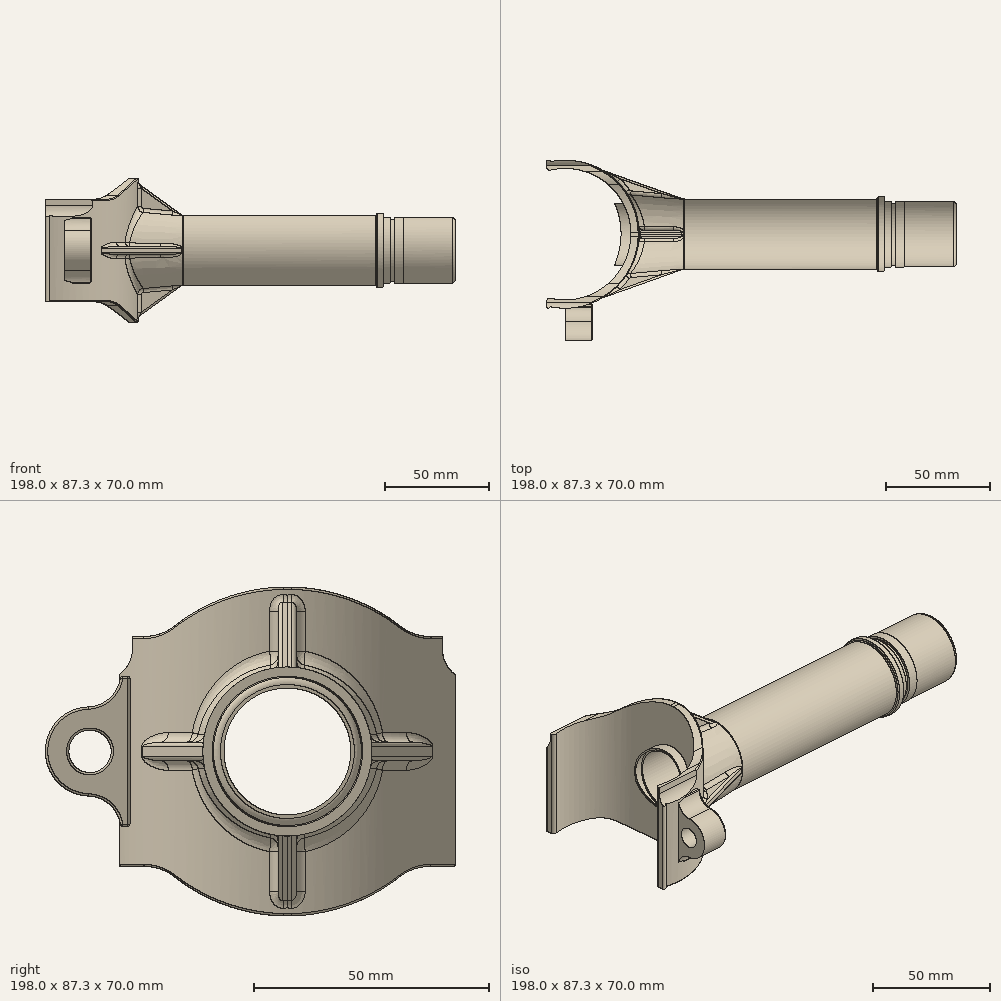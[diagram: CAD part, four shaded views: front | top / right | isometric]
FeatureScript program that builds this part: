
annotation { "Feature Type Name" : "Feature", "Feature Type Description" : "" }
export const myFeature = defineFeature(function(context is Context, id is Id, definition is map)
    precondition{}
    {
        {
            var Q0;
            Q0=qCreatedBy(makeId("Right.planeOp"),FACE);
            var sketch = newSketch(context, id + "F0", { "sketchPlane" : qUnion([Q0])});
            skLineSegment(sketch, "E0", {"start": v(0, 105.09) * mm, "end": v(0, -109.38) * mm, "construction": true});
            skLineSegment(sketch, "E1", {"start": v(-124.9, 0) * mm, "end": v(126.38, 0) * mm, "construction": true});
            skLineSegment(sketch, "E2.0", {"start": v(-42, 105.09) * mm, "end": v(-42, -109.38) * mm, "construction": true});
            skArc(sketch, "E3", {"start": v(-42.29, 9.5) * mm, "mid": v(-51.5, 0) * mm, "end": v(-42.29, -9.5) * mm});
            skLineSegment(sketch, "E4.0", {"start": v(-124.9, 24.5) * mm, "end": v(-30.22, 24.5) * mm});
            skLineSegment(sketch, "E5.MirrorCS", {"start": v(-124.9, -24.5) * mm, "end": v(-30.22, -24.5) * mm});
            skLineSegment(sketch, "E6.0", {"start": v(-124.9, -3.7) * mm, "end": v(126.38, -3.7) * mm, "construction": true});
            skArc(sketch, "E7.trimOffspring", {"start": v(24.01, 26.66) * mm, "mid": v(0, 35.01) * mm, "end": v(-24.01, 26.66) * mm});
            skPoint(sketch, "E8.newPointB", {"position": v(126.68, 24.5) * mm});
            skArc(sketch, "E8.filletArc", {"start": v(-30.22, 24.5) * mm, "mid": v(-26.93, 25.05) * mm, "end": v(-24.01, 26.66) * mm});
            skArc(sketch, "E9.MirrorCS", {"start": v(30.22, 24.5) * mm, "mid": v(26.93, 25.05) * mm, "end": v(24.01, 26.66) * mm});
            skLineSegment(sketch, "E10.MirrorCS", {"start": v(124.9, 24.5) * mm, "end": v(30.22, 24.5) * mm});
            skLineSegment(sketch, "E11", {"start": v(-68.14, 24.5) * mm, "end": v(-68.14, 50.23) * mm});
            skLineSegment(sketch, "E12", {"start": v(-68.14, 50.23) * mm, "end": v(68.14, 50.23) * mm});
            skLineSegment(sketch, "E13.MirrorCS", {"start": v(68.14, 24.5) * mm, "end": v(68.14, 50.23) * mm});
            skArc(sketch, "E14.MirrorCS", {"start": v(30.22, -24.5) * mm, "mid": v(26.93, -25.05) * mm, "end": v(24.01, -26.66) * mm});
            skArc(sketch, "E15.MirrorCS", {"start": v(24.01, -26.66) * mm, "mid": v(0, -35.01) * mm, "end": v(-24.01, -26.66) * mm});
            skArc(sketch, "E16.MirrorCS", {"start": v(-30.22, -24.5) * mm, "mid": v(-26.93, -25.05) * mm, "end": v(-24.01, -26.66) * mm});
            skLineSegment(sketch, "E17.MirrorCS", {"start": v(-68.14, -24.5) * mm, "end": v(-68.14, -50.23) * mm});
            skLineSegment(sketch, "E18.MirrorCS", {"start": v(-68.14, -50.23) * mm, "end": v(68.14, -50.23) * mm});
            skLineSegment(sketch, "E19.MirrorCS", {"start": v(68.14, -24.5) * mm, "end": v(68.14, -50.23) * mm});
            skLineSegment(sketch, "E20.trimOffspring", {"start": v(30.22, -24.5) * mm, "end": v(126.68, -24.5) * mm});
            skLineSegment(sketch, "E21.0", {"start": v(-33.5, 15.5) * mm, "end": v(-33.5, -15.5) * mm});
            skLineSegment(sketch, "E22.0", {"start": v(-35.07, 16) * mm, "end": v(-34, 16) * mm});
            skPoint(sketch, "E23.visualSharp", {"position": v(-35.5, 6.93) * mm});
            skArc(sketch, "E23.filletArc", {"start": v(-42.29, 9.5) * mm, "mid": v(-37.81, 11.3) * mm, "end": v(-35.56, 15.57) * mm});
            skArc(sketch, "E24.filletArc", {"start": v(-35.07, 16) * mm, "mid": v(-35.4, 15.88) * mm, "end": v(-35.56, 15.57) * mm});
            skArc(sketch, "E25.filletArc", {"start": v(-33.5, 15.5) * mm, "mid": v(-33.65, 15.85) * mm, "end": v(-34, 16) * mm});
            skArc(sketch, "E26.MirrorCS", {"start": v(-42.29, -9.5) * mm, "mid": v(-37.81, -11.3) * mm, "end": v(-35.56, -15.57) * mm});
            skArc(sketch, "E27.MirrorCS", {"start": v(-35.07, -16) * mm, "mid": v(-35.4, -15.88) * mm, "end": v(-35.56, -15.57) * mm});
            skLineSegment(sketch, "E28.MirrorCS", {"start": v(-35.07, -16) * mm, "end": v(-34, -16) * mm});
            skArc(sketch, "E29.MirrorCS", {"start": v(-33.5, -15.5) * mm, "mid": v(-33.65, -15.85) * mm, "end": v(-34, -16) * mm});
            skLineSegment(sketch, "E30.trimOffspring", {"start": v(-33.5, -24.5) * mm, "end": v(-33.5, -109.38) * mm});
            skCircle(sketch, "E31", {"center": v(-42, 0) * mm, "radius": 4.5 * mm});
            skArc(sketch, "E32.MirrorCS", {"start": v(33.5, 15.5) * mm, "mid": v(33.65, 15.85) * mm, "end": v(34, 16) * mm});
            skArc(sketch, "E33.MirrorCS", {"start": v(35.07, 16) * mm, "mid": v(35.4, 15.88) * mm, "end": v(35.56, 15.57) * mm});
            skArc(sketch, "E34.MirrorCS", {"start": v(35.07, -16) * mm, "mid": v(35.4, -15.88) * mm, "end": v(35.56, -15.57) * mm});
            skLineSegment(sketch, "E35.MirrorCS", {"start": v(35.07, 16) * mm, "end": v(34, 16) * mm});
            skLineSegment(sketch, "E36.MirrorCS", {"start": v(35.07, -16) * mm, "end": v(34, -16) * mm});
            skArc(sketch, "E37.MirrorCS", {"start": v(33.5, -15.5) * mm, "mid": v(33.65, -15.85) * mm, "end": v(34, -16) * mm});
            skCircle(sketch, "E38.MirrorC", {"center": v(42, 0) * mm, "radius": 4.5 * mm});
            skPoint(sketch, "E39.MirrorP", {"position": v(35.5, 6.93) * mm});
            skLineSegment(sketch, "E40.MirrorCS", {"start": v(33.5, 15.5) * mm, "end": v(33.5, -15.5) * mm});
            skArc(sketch, "E41.MirrorCS", {"start": v(42.29, 9.5) * mm, "mid": v(37.81, 11.3) * mm, "end": v(35.56, 15.57) * mm});
            skArc(sketch, "E42.MirrorCS", {"start": v(42.29, -9.5) * mm, "mid": v(37.81, -11.3) * mm, "end": v(35.56, -15.57) * mm});
            skArc(sketch, "E43.MirrorCS", {"start": v(42.29, 9.5) * mm, "mid": v(51.5, 0) * mm, "end": v(42.29, -9.5) * mm});
            skSolve(sketch);
        }
        {
            var Q0;
            Q0=qCreatedBy(makeId("Top.planeOp"),FACE);
            var sketch = newSketch(context, id + "F1", { "sketchPlane" : qUnion([Q0])});
            skLineSegment(sketch, "E44", {"start": v(-75.74, 0) * mm, "end": v(95.85, 0) * mm, "construction": true});
            skLineSegment(sketch, "E45", {"start": v(0, 79.62) * mm, "end": v(0, -83.5) * mm, "construction": true});
            skArc(sketch, "E46", {"start": v(-7.02, -30.96) * mm, "mid": v(31.75, 0) * mm, "end": v(-7.02, 30.96) * mm});
            skArc(sketch, "E47.0", {"start": v(-8.99, 34.6) * mm, "mid": v(-8.99, 34.6) * mm, "end": v(-9, 34.6) * mm});
            skLineSegment(sketch, "E48.0", {"start": v(-8, 79.62) * mm, "end": v(-8, -83.5) * mm, "construction": true});
            skLineSegment(sketch, "E49.0", {"start": v(-75.74, 34.77) * mm, "end": v(95.85, 34.77) * mm, "construction": true});
            skArc(sketch, "E50", {"start": v(-7.04, 35.05) * mm, "mid": v(-8.22, 35.74) * mm, "end": v(-8.99, 34.6) * mm});
            skLineSegment(sketch, "E51", {"start": v(-8.85, 32.33) * mm, "end": v(-9, 34.7) * mm});
            skArc(sketch, "E52.trimOffspring", {"start": v(-9, -34.6) * mm, "mid": v(-8.99, -34.6) * mm, "end": v(-8.99, -34.6) * mm});
            skLineSegment(sketch, "E53.MirrorCS", {"start": v(-8.85, -32.33) * mm, "end": v(-9, -34.7) * mm});
            skArc(sketch, "E54.MirrorC", {"start": v(-7.04, -35.05) * mm, "mid": v(-8.17, -35.76) * mm, "end": v(-9, -34.7) * mm});
            skPoint(sketch, "E55.newPointA", {"position": v(-8.7, 30) * mm});
            skArc(sketch, "E55.filletArc", {"start": v(-8.85, 32.33) * mm, "mid": v(-8.25, 31.23) * mm, "end": v(-7.02, 30.96) * mm});
            skPoint(sketch, "E56.newPointA", {"position": v(-8.7, -30) * mm});
            skArc(sketch, "E56.filletArc", {"start": v(-7.02, -30.96) * mm, "mid": v(-8.25, -31.23) * mm, "end": v(-8.85, -32.33) * mm});
            skArc(sketch, "E57.trimOffspring", {"start": v(-7.04, -35.05) * mm, "mid": v(35.75, 0) * mm, "end": v(-7.04, 35.05) * mm});
            skSolve(sketch);
        }
        {
            var Q0;
            Q0=makeQuery(id+"F1.imprint","IMPRINT",FACE,{"disambiguationData":[TD([[makeQuery(id+"F1.imprint","IMPRINT",EDGE,{"derivedFrom":sQuery(id+"F1.wireOp",EDGE,"E46")}),-1.0]])]});
            extrude(context, id + "F2", {"entities" : qUnion([Q0]), "endBound" : BoundingType.SYMMETRIC, "depth" : 70 * mm, "offsetDistance" : 25 * mm});
        }
        {
            var Q0;
            Q0=makeQuery(id+"F0.imprint","IMPRINT",FACE,{"disambiguationData":[TD([[makeQuery(id+"F0.imprint","IMPRINT",EDGE,{"derivedFrom":sQuery(id+"F0.wireOp",EDGE,"E7.trimOffspring")}),-1.0]])]});
            var Q1;
            {var subQ0=sQuery(id+"F0.wireOp",EDGE,"E14.MirrorCS");Q1=makeQuery(id+"F0.imprint","IMPRINT",FACE,{"disambiguationData":[TD([[makeQuery(id+"F0.imprint","IMPRINT",EDGE,{"derivedFrom":subQ0}),1.0]])]});}
            var Q2;
            {var subQ5=sQuery(id+"F0.wireOp",EDGE,"E17.MirrorCS");Q2=makeQuery(id+"F0.imprint","IMPRINT",FACE,{"disambiguationData":[TD([[makeQuery(id+"F0.imprint","IMPRINT",EDGE,{"derivedFrom":subQ5}),1.0]])]});}
            extrude(context, id + "F3", {"entities" : qUnion([Q0, Q1, Q2]), "operationType" : NewBodyOperationType.REMOVE, "endBound" : BoundingType.SYMMETRIC, "depth" : 100 * mm, "offsetDistance" : 25 * mm});
        }
        {
            var Q0;
            Q0=makeQuery(id+"F0.imprint","IMPRINT",FACE,{"disambiguationData":[TD([[makeQuery(id+"F0.imprint","IMPRINT",EDGE,{"derivedFrom":sQuery(id+"F0.wireOp",EDGE,"E3")}),1.0]])]});
            var Q1;
            Q1=makeQuery(id+"F0.imprint","IMPRINT",FACE,{"disambiguationData":[TD([[makeQuery(id+"F0.imprint","IMPRINT",EDGE,{"derivedFrom":sQuery(id+"F0.wireOp",EDGE,"E32.MirrorCS")}),-1.0]])]});
            extrude(context, id + "F4", {"entities" : qUnion([Q0, Q1]), "operationType" : NewBodyOperationType.ADD, "depth" : 13 * mm, "offsetDistance" : 25 * mm});
        }
        {
            var Q0;
            Q0=makeQuery(id+"F4.opExtrude","CAP_FACE",FACE,{"disambiguationData":[OSD([sQuery(id+"F0.wireOp",EDGE,"E3"),sQuery(id+"F0.wireOp",EDGE,"E21.0"),sQuery(id+"F0.wireOp",EDGE,"E22.0"),sQuery(id+"F0.wireOp",EDGE,"E23.filletArc"),sQuery(id+"F0.wireOp",EDGE,"E24.filletArc"),sQuery(id+"F0.wireOp",EDGE,"E25.filletArc"),sQuery(id+"F0.wireOp",EDGE,"E26.MirrorCS"),sQuery(id+"F0.wireOp",EDGE,"E27.MirrorCS"),sQuery(id+"F0.wireOp",EDGE,"E28.MirrorCS"),sQuery(id+"F0.wireOp",EDGE,"E29.MirrorCS"),sQuery(id+"F0.wireOp",EDGE,"E31")])],"isStart":false});
            var Q1;
            Q1=makeQuery(id+"F4.opExtrude","CAP_FACE",FACE,{"disambiguationData":[OSD([sQuery(id+"F0.wireOp",EDGE,"E32.MirrorCS"),sQuery(id+"F0.wireOp",EDGE,"E33.MirrorCS"),sQuery(id+"F0.wireOp",EDGE,"E34.MirrorCS"),sQuery(id+"F0.wireOp",EDGE,"E35.MirrorCS"),sQuery(id+"F0.wireOp",EDGE,"E36.MirrorCS"),sQuery(id+"F0.wireOp",EDGE,"E37.MirrorCS"),sQuery(id+"F0.wireOp",EDGE,"E38.MirrorC"),sQuery(id+"F0.wireOp",EDGE,"E40.MirrorCS"),sQuery(id+"F0.wireOp",EDGE,"E41.MirrorCS"),sQuery(id+"F0.wireOp",EDGE,"E42.MirrorCS"),sQuery(id+"F0.wireOp",EDGE,"E43.MirrorCS")])],"isStart":false});
            fillet(context, id + "F5", {"entities" : qUnion([Q0, Q1]), "radius" : 0.5 * mm, "tangentPropagation" : true, "allowEdgeOverflow" : false});
        }
        {
            var Q0;
            Q0=qCreatedBy(makeId("Right.planeOp"),FACE);
            var sketch = newSketch(context, id + "F6", { "sketchPlane" : qUnion([Q0])});
            skLineSegment(sketch, "E58", {"start": v(0, 44.7) * mm, "end": v(0, -6.12) * mm, "construction": true});
            skLineSegment(sketch, "E59", {"start": v(-3.2, 0) * mm, "end": v(58.54, 0) * mm, "construction": true});
            skArc(sketch, "E60", {"start": v(33, 21.71) * mm, "mid": v(33.8, 18.54) * mm, "end": v(36, 16.13) * mm});
            skLineSegment(sketch, "E61.0", {"start": v(36, 24.5) * mm, "end": v(36, 16.13) * mm});
            skLineSegment(sketch, "E62.trimOffspring", {"start": v(33, 24.5) * mm, "end": v(36, 24.5) * mm});
            skLineSegment(sketch, "E63", {"start": v(33, 21.71) * mm, "end": v(33, 24.5) * mm});
            skLineSegment(sketch, "E64.MirrorCS", {"start": v(-36, 24.5) * mm, "end": v(-36, 16.13) * mm});
            skArc(sketch, "E65.MirrorCS", {"start": v(-33, 21.71) * mm, "mid": v(-33.8, 18.54) * mm, "end": v(-36, 16.13) * mm});
            skLineSegment(sketch, "E66.MirrorCS", {"start": v(-33, 24.5) * mm, "end": v(-36, 24.5) * mm});
            skLineSegment(sketch, "E67.MirrorCS", {"start": v(-33, 21.71) * mm, "end": v(-33, 24.5) * mm});
            skSolve(sketch);
        }
        {
            var Q0;
            Q0=makeQuery(id+"F6.imprint","IMPRINT",FACE,{"disambiguationData":[TD([[makeQuery(id+"F6.imprint","IMPRINT",EDGE,{"derivedFrom":sQuery(id+"F6.wireOp",EDGE,"E64.MirrorCS")}),1.0]])]});
            var Q1;
            Q1=makeQuery(id+"F6.imprint","IMPRINT",FACE,{"disambiguationData":[TD([[makeQuery(id+"F6.imprint","IMPRINT",EDGE,{"derivedFrom":sQuery(id+"F6.wireOp",EDGE,"E60")}),1.0]])]});
            extrude(context, id + "F7", {"entities" : qUnion([Q0, Q1]), "operationType" : NewBodyOperationType.REMOVE, "endBound" : BoundingType.SYMMETRIC, "depth" : 100 * mm, "offsetDistance" : 25 * mm});
        }
        {
            var Q0;
            Q0=makeQuery(id+"F7.boolean.opBoolean","COPY",EDGE,{"derivedFrom":makeQuery(id+"F7.opExtrude","SWEPT_EDGE",EDGE,{"disambiguationData":[OSD([sQuery(id+"F6.wireOp",EDGE,"E66.MirrorCS"),sQuery(id+"F6.wireOp",EDGE,"E67.MirrorCS")])]})});
            var Q1;
            Q1=makeQuery(id+"F3.boolean.opBoolean","INTERSECT",EDGE,{"derivedFrom":[makeQuery(id+"F2.opExtrude","SWEPT_FACE",FACE,{"disambiguationData":[OSD([sQuery(id+"F1.wireOp",EDGE,"E57.trimOffspring")])]}),makeQuery(id+"F3.opExtrude","SWEPT_FACE",FACE,{"disambiguationData":[OSD([sQuery(id+"F0.wireOp",EDGE,"E4.0")])]})]});
            var Q2;
            Q2=makeQuery(id+"F3.boolean.opBoolean","INTERSECT",EDGE,{"derivedFrom":[makeQuery(id+"F2.opExtrude","SWEPT_FACE",FACE,{"disambiguationData":[OSD([sQuery(id+"F1.wireOp",EDGE,"E57.trimOffspring")])]}),makeQuery(id+"F3.opExtrude","SWEPT_FACE",FACE,{"disambiguationData":[OSD([sQuery(id+"F0.wireOp",EDGE,"E8.filletArc")])]})]});
            var Q3;
            Q3=makeQuery(id+"F2.opExtrude","CAP_EDGE",EDGE,{"disambiguationData":[OSD([sQuery(id+"F1.wireOp",EDGE,"E57.trimOffspring")])],"isStart":false});
            var Q4;
            Q4=makeQuery(id+"F3.boolean.opBoolean","INTERSECT",EDGE,{"disambiguationData":[OD(0.0)],"derivedFrom":[makeQuery(id+"F2.opExtrude","SWEPT_FACE",FACE,{"disambiguationData":[OSD([sQuery(id+"F1.wireOp",EDGE,"E57.trimOffspring")])]}),makeQuery(id+"F3.opExtrude","SWEPT_FACE",FACE,{"disambiguationData":[OSD([sQuery(id+"F0.wireOp",EDGE,"E7.trimOffspring")])]})]});
            var Q5;
            Q5=makeQuery(id+"F3.boolean.opBoolean","INTERSECT",EDGE,{"disambiguationData":[OD(1.0)],"derivedFrom":[makeQuery(id+"F2.opExtrude","SWEPT_FACE",FACE,{"disambiguationData":[OSD([sQuery(id+"F1.wireOp",EDGE,"E57.trimOffspring")])]}),makeQuery(id+"F3.opExtrude","SWEPT_FACE",FACE,{"disambiguationData":[OSD([sQuery(id+"F0.wireOp",EDGE,"E7.trimOffspring")])]})]});
            var Q6;
            Q6=makeQuery(id+"F3.boolean.opBoolean","INTERSECT",EDGE,{"derivedFrom":[makeQuery(id+"F2.opExtrude","SWEPT_FACE",FACE,{"disambiguationData":[OSD([sQuery(id+"F1.wireOp",EDGE,"E57.trimOffspring")])]}),makeQuery(id+"F3.opExtrude","SWEPT_FACE",FACE,{"disambiguationData":[OSD([sQuery(id+"F0.wireOp",EDGE,"E9.MirrorCS")])]})]});
            var Q7;
            Q7=makeQuery(id+"F3.boolean.opBoolean","INTERSECT",EDGE,{"derivedFrom":[makeQuery(id+"F2.opExtrude","SWEPT_FACE",FACE,{"disambiguationData":[OSD([sQuery(id+"F1.wireOp",EDGE,"E57.trimOffspring")])]}),makeQuery(id+"F3.opExtrude","SWEPT_FACE",FACE,{"disambiguationData":[OSD([sQuery(id+"F0.wireOp",EDGE,"E10.MirrorCS")])]})]});
            var Q8;
            Q8=makeQuery(id+"F7.boolean.opBoolean","COPY",EDGE,{"derivedFrom":makeQuery(id+"F7.opExtrude","SWEPT_EDGE",EDGE,{"disambiguationData":[OSD([sQuery(id+"F6.wireOp",EDGE,"E62.trimOffspring"),sQuery(id+"F6.wireOp",EDGE,"E63")])]})});
            var Q9;
            Q9=makeQuery(id+"FyGXZyxvwHZdhN8_1.1.F7.boolean.opBoolean","COPY",EDGE,{"derivedFrom":makeQuery(id+"FyGXZyxvwHZdhN8_1.1.F7.opExtrude","SWEPT_EDGE",EDGE,{"disambiguationData":[OSD([sQuery(id+"F6.wireOp",EDGE,"E66.MirrorCS"),sQuery(id+"F6.wireOp",EDGE,"E67.MirrorCS")])]})});
            var Q10;
            Q10=makeQuery(id+"F3.boolean.opBoolean","INTERSECT",EDGE,{"derivedFrom":[makeQuery(id+"F2.opExtrude","SWEPT_FACE",FACE,{"disambiguationData":[OSD([sQuery(id+"F1.wireOp",EDGE,"E57.trimOffspring")])]}),makeQuery(id+"F3.opExtrude","SWEPT_FACE",FACE,{"disambiguationData":[OSD([sQuery(id+"F0.wireOp",EDGE,"E5.MirrorCS")])]})]});
            var Q11;
            Q11=makeQuery(id+"F3.boolean.opBoolean","INTERSECT",EDGE,{"derivedFrom":[makeQuery(id+"F2.opExtrude","SWEPT_FACE",FACE,{"disambiguationData":[OSD([sQuery(id+"F1.wireOp",EDGE,"E57.trimOffspring")])]}),makeQuery(id+"F3.opExtrude","SWEPT_FACE",FACE,{"disambiguationData":[OSD([sQuery(id+"F0.wireOp",EDGE,"E16.MirrorCS")])]})]});
            var Q12;
            Q12=makeQuery(id+"F3.boolean.opBoolean","INTERSECT",EDGE,{"disambiguationData":[OD(1.0)],"derivedFrom":[makeQuery(id+"F2.opExtrude","SWEPT_FACE",FACE,{"disambiguationData":[OSD([sQuery(id+"F1.wireOp",EDGE,"E57.trimOffspring")])]}),makeQuery(id+"F3.opExtrude","SWEPT_FACE",FACE,{"disambiguationData":[OSD([sQuery(id+"F0.wireOp",EDGE,"E15.MirrorCS")])]})]});
            var Q13;
            Q13=makeQuery(id+"F2.opExtrude","CAP_EDGE",EDGE,{"disambiguationData":[OSD([sQuery(id+"F1.wireOp",EDGE,"E57.trimOffspring")])],"isStart":true});
            var Q14;
            Q14=makeQuery(id+"F3.boolean.opBoolean","INTERSECT",EDGE,{"disambiguationData":[OD(0.0)],"derivedFrom":[makeQuery(id+"F2.opExtrude","SWEPT_FACE",FACE,{"disambiguationData":[OSD([sQuery(id+"F1.wireOp",EDGE,"E57.trimOffspring")])]}),makeQuery(id+"F3.opExtrude","SWEPT_FACE",FACE,{"disambiguationData":[OSD([sQuery(id+"F0.wireOp",EDGE,"E15.MirrorCS")])]})]});
            var Q15;
            Q15=makeQuery(id+"F3.boolean.opBoolean","INTERSECT",EDGE,{"derivedFrom":[makeQuery(id+"F2.opExtrude","SWEPT_FACE",FACE,{"disambiguationData":[OSD([sQuery(id+"F1.wireOp",EDGE,"E57.trimOffspring")])]}),makeQuery(id+"F3.opExtrude","SWEPT_FACE",FACE,{"disambiguationData":[OSD([sQuery(id+"F0.wireOp",EDGE,"E14.MirrorCS")])]})]});
            var Q16;
            Q16=makeQuery(id+"F3.boolean.opBoolean","INTERSECT",EDGE,{"derivedFrom":[makeQuery(id+"F2.opExtrude","SWEPT_FACE",FACE,{"disambiguationData":[OSD([sQuery(id+"F1.wireOp",EDGE,"E57.trimOffspring")])]}),makeQuery(id+"F3.opExtrude","SWEPT_FACE",FACE,{"disambiguationData":[OSD([sQuery(id+"F0.wireOp",EDGE,"E20.trimOffspring")])]})]});
            var Q17;
            Q17=makeQuery(id+"FyGXZyxvwHZdhN8_1.1.F7.boolean.opBoolean","COPY",EDGE,{"derivedFrom":makeQuery(id+"FyGXZyxvwHZdhN8_1.1.F7.opExtrude","SWEPT_EDGE",EDGE,{"disambiguationData":[OSD([sQuery(id+"F6.wireOp",EDGE,"E62.trimOffspring"),sQuery(id+"F6.wireOp",EDGE,"E63")])]})});
            fillet(context, id + "F8", {"entities" : qUnion([Q0, Q1, Q2, Q3, Q4, Q5, Q6, Q7, Q8, Q9, Q10, Q11, Q12, Q13, Q14, Q15, Q16, Q17]), "radius" : 0.5 * mm, "tangentPropagation" : true, "allowEdgeOverflow" : false});
        }
        {
            var Q0;
            Q0=qCreatedBy(makeId("Front.planeOp"),FACE);
            var sketch = newSketch(context, id + "F9", { "sketchPlane" : qUnion([Q0])});
            skLineSegment(sketch, "E68", {"start": v(0, 48.66) * mm, "end": v(0, -47.81) * mm, "construction": true});
            skLineSegment(sketch, "E69", {"start": v(-80.31, 0) * mm, "end": v(431.9, 0) * mm, "construction": true});
            skLineSegment(sketch, "E70.0", {"start": v(24.55, 19.98) * mm, "end": v(24.55, 0) * mm});
            skLineSegment(sketch, "E71.0", {"start": v(189, 15.75) * mm, "end": v(189, 0) * mm});
            skLineSegment(sketch, "E72", {"start": v(189, 15.75) * mm, "end": v(164, 15.75) * mm});
            skLineSegment(sketch, "E73", {"start": v(164, 15.75) * mm, "end": v(164, 16) * mm});
            skLineSegment(sketch, "E74", {"start": v(159.5, 16) * mm, "end": v(159.5, 15) * mm});
            skLineSegment(sketch, "E75", {"start": v(159.5, 15) * mm, "end": v(157.5, 15) * mm});
            skLineSegment(sketch, "E76", {"start": v(157.5, 15) * mm, "end": v(157.5, 16) * mm});
            skLineSegment(sketch, "E77", {"start": v(157.5, 16) * mm, "end": v(154, 16) * mm});
            skLineSegment(sketch, "E78", {"start": v(154, 16) * mm, "end": v(154, 18) * mm});
            skLineSegment(sketch, "E79", {"start": v(154, 18) * mm, "end": v(151, 18) * mm});
            skLineSegment(sketch, "E80", {"start": v(151, 18) * mm, "end": v(151, 17) * mm});
            skLineSegment(sketch, "E81", {"start": v(151, 17) * mm, "end": v(57.53, 17) * mm});
            skLineSegment(sketch, "E82", {"start": v(57.53, 17) * mm, "end": v(24.55, 19.98) * mm});
            skLineSegment(sketch, "E83", {"start": v(159.5, 16) * mm, "end": v(164, 16) * mm});
            skLineSegment(sketch, "E84", {"start": v(24.55, 0) * mm, "end": v(189, 0) * mm});
            skSolve(sketch);
        }
        {
            var Q0;
            Q0=makeQuery(id+"F9.imprint","IMPRINT",FACE,{"disambiguationData":[TD([[makeQuery(id+"F9.imprint","IMPRINT",EDGE,{"derivedFrom":sQuery(id+"F9.wireOp",EDGE,"E70.0")}),1.0]])]});
            var Q1;
            Q1=sQuery(id+"F9.wireOp",EDGE,"E69");
            revolve(context, id + "F10", {"operationType" : NewBodyOperationType.ADD, "surfaceOperationType" : NewSurfaceOperationType.NEW, "entities" : qUnion([Q0]), "axis" : qUnion([Q1]), "revolveType" : RevolveType.FULL});
        }
        {
            var Q0;
            Q0=qCreatedBy(makeId("Top.planeOp"),FACE);
            var sketch = newSketch(context, id + "F11", { "sketchPlane" : qUnion([Q0])});
            skCircle(sketch, "E85", {"center": v(0, 0) * mm, "radius": 31.75 * mm});
            skLineSegment(sketch, "E86", {"start": v(0, -53.07) * mm, "end": v(0, 52.67) * mm, "construction": true});
            skLineSegment(sketch, "E87.0", {"start": v(27, -53.07) * mm, "end": v(27, 52.67) * mm, "construction": true});
            skLineSegment(sketch, "E88", {"start": v(-10.9, 0) * mm, "end": v(40.63, 0) * mm, "construction": true});
            skLineSegment(sketch, "E89", {"start": v(23.2, 16.39) * mm, "end": v(23.2, -16.39) * mm});
            skLineSegment(sketch, "E90.0", {"start": v(-10.29, -53.07) * mm, "end": v(-10.29, 52.67) * mm, "construction": true});
            skArc(sketch, "E91.trimOffspring", {"start": v(23.2, -16.39) * mm, "mid": v(27, 0) * mm, "end": v(23.2, 16.39) * mm});
            skSolve(sketch);
        }
        {
            var Q0;
            Q0=makeQuery(id+"F11.imprint","IMPRINT",FACE,{"disambiguationData":[TD([[makeQuery(id+"F11.imprint","IMPRINT",EDGE,{"derivedFrom":sQuery(id+"F11.wireOp",EDGE,"E85")}),1.0]])]});
            extrude(context, id + "F12", {"entities" : qUnion([Q0]), "operationType" : NewBodyOperationType.REMOVE, "endBound" : BoundingType.SYMMETRIC, "depth" : 60 * mm, "offsetDistance" : 25 * mm});
        }
        {
            var Q0;
            Q0=makeQuery(id+"F10.boolean.opBoolean","INTERSECT",EDGE,{"derivedFrom":[makeQuery(id+"F2.opExtrude","SWEPT_FACE",FACE,{"disambiguationData":[OSD([sQuery(id+"F1.wireOp",EDGE,"E57.trimOffspring")])]}),makeQuery(id+"F10.opRevolve","SWEPT_FACE",FACE,{"disambiguationData":[OSD([sQuery(id+"F9.wireOp",EDGE,"E82")])]})]});
            var Q1;
            Q1=makeQuery(id+"F10.opRevolve","SWEPT_EDGE",EDGE,{"disambiguationData":[OSD([sQuery(id+"F9.wireOp",EDGE,"E81"),sQuery(id+"F9.wireOp",EDGE,"E82")])]});
            fillet(context, id + "F13", {"entities" : qUnion([Q0, Q1]), "radius" : 3 * mm, "tangentPropagation" : true, "allowEdgeOverflow" : false});
        }
        {
            var Q0;
            Q0=makeQuery(id+"F10.opRevolve","SWEPT_EDGE",EDGE,{"disambiguationData":[OSD([sQuery(id+"F9.wireOp",EDGE,"E79"),sQuery(id+"F9.wireOp",EDGE,"E80")])]});
            var Q1;
            Q1=makeQuery(id+"F10.opRevolve","SWEPT_EDGE",EDGE,{"disambiguationData":[OSD([sQuery(id+"F9.wireOp",EDGE,"E80"),sQuery(id+"F9.wireOp",EDGE,"E81")])]});
            fillet(context, id + "F14", {"entities" : qUnion([Q0, Q1]), "radius" : 0.5 * mm, "tangentPropagation" : true, "allowEdgeOverflow" : false});
        }
        {
            var Q0;
            Q0=qCreatedBy(makeId("Right.planeOp"),FACE);
            cPlane(context, id + "F15", {"entities" : qUnion([Q0]), "cplaneType" : CPlaneType.OFFSET, "offset" : 32 * mm, "width" : 150 * mm, "height" : 150 * mm});
        }
        {
            var Q0;
            Q0=qCreatedBy(id+"F15.planeOp",FACE);
            var sketch = newSketch(context, id + "F16", { "sketchPlane" : qUnion([Q0])});
            skCircle(sketch, "E92", {"center": v(0, 0) * mm, "radius": 15 * mm});
            skSolve(sketch);
        }
        {
            var Q0;
            Q0=makeQuery(id+"F16.imprint","IMPRINT",FACE,{"disambiguationData":[TD([[makeQuery(id+"F16.imprint","IMPRINT",EDGE,{"derivedFrom":sQuery(id+"F16.wireOp",EDGE,"E92")}),1.0]])]});
            extrude(context, id + "F17", {"entities" : qUnion([Q0]), "operationType" : NewBodyOperationType.ADD, "oppositeDirection" : true, "depth" : 8 * mm, "offsetDistance" : 25 * mm});
        }
        {
            var Q0;
            Q0=makeQuery(id+"F17.opExtrude","CAP_FACE",FACE,{"disambiguationData":[OSD([sQuery(id+"F16.wireOp",EDGE,"E92")])],"isStart":false});
            fillet(context, id + "F18", {"entities" : qUnion([Q0]), "radius" : 0.3 * mm, "tangentPropagation" : true, "allowEdgeOverflow" : false});
        }
        {
            var Q0;
            Q0=makeQuery(id+"F17.opExtrude","CAP_FACE",FACE,{"disambiguationData":[OSD([sQuery(id+"F16.wireOp",EDGE,"E92")])],"isStart":false});
            var sketch = newSketch(context, id + "F19", { "sketchPlane" : qUnion([Q0])});
            skCircle(sketch, "E93", {"center": v(0, 0) * mm, "radius": 14.3 * mm});
            skSolve(sketch);
        }
        {
            var Q0;
            Q0=makeQuery(id+"F19.imprint","IMPRINT",FACE,{"disambiguationData":[TD([[makeQuery(id+"F19.imprint","IMPRINT",EDGE,{"derivedFrom":sQuery(id+"F19.wireOp",EDGE,"E93")}),1.0]])]});
            extrude(context, id + "F20", {"entities" : qUnion([Q0]), "operationType" : NewBodyOperationType.REMOVE, "oppositeDirection" : true, "depth" : 3.5 * mm, "offsetDistance" : 25 * mm});
        }
        {
            var Q0;
            Q0=makeQuery(id+"F11.imprint","IMPRINT",FACE,{"disambiguationData":[TD([[makeQuery(id+"F11.imprint","IMPRINT",EDGE,{"derivedFrom":sQuery(id+"F11.wireOp",EDGE,"E89")}),1.0]])]});
            extrude(context, id + "F21", {"entities" : qUnion([Q0]), "operationType" : NewBodyOperationType.REMOVE, "endBound" : BoundingType.SYMMETRIC, "oppositeDirection" : true, "depth" : 50 * mm, "offsetDistance" : 25 * mm});
        }
        {
            var Q0;
            Q0=makeQuery(id+"F20.boolean.opBoolean","COPY",FACE,{"derivedFrom":makeQuery(id+"F20.opExtrude","CAP_FACE",FACE,{"disambiguationData":[OSD([sQuery(id+"F19.wireOp",EDGE,"E93")])],"isStart":false})});
            var sketch = newSketch(context, id + "F22", { "sketchPlane" : qUnion([Q0])});
            skCircle(sketch, "E94", {"center": v(0, 0) * mm, "radius": 13.5 * mm});
            skSolve(sketch);
        }
        {
            var Q0;
            Q0=makeQuery(id+"F22.imprint","IMPRINT",FACE,{"disambiguationData":[TD([[makeQuery(id+"F22.imprint","IMPRINT",EDGE,{"derivedFrom":sQuery(id+"F22.wireOp",EDGE,"E94")}),1.0]])]});
            extrude(context, id + "F23", {"entities" : qUnion([Q0]), "operationType" : NewBodyOperationType.REMOVE, "oppositeDirection" : true, "depth" : 161.5 * mm, "offsetDistance" : 25 * mm});
        }
        {
            var Q0;
            Q0=makeQuery(id+"F10.opRevolve","SWEPT_EDGE",EDGE,{"disambiguationData":[OSD([sQuery(id+"F9.wireOp",EDGE,"E71.0"),sQuery(id+"F9.wireOp",EDGE,"E72")])]});
            fillet(context, id + "F24", {"entities" : qUnion([Q0]), "radius" : 1.5 * mm, "tangentPropagation" : true, "allowEdgeOverflow" : false});
        }
        {
            var Q0;
            Q0=qCreatedBy(makeId("Front.planeOp"),FACE);
            var sketch = newSketch(context, id + "F25", { "sketchPlane" : qUnion([Q0])});
            skLineSegment(sketch, "E95", {"start": v(35, 32.81) * mm, "end": v(58.66, 15.7) * mm});
            skLineSegment(sketch, "E96", {"start": v(-20.71, 0) * mm, "end": v(79.12, 0) * mm, "construction": true});
            skLineSegment(sketch, "E97.0", {"start": v(-20.71, 17) * mm, "end": v(79.12, 17) * mm});
            skLineSegment(sketch, "E98", {"start": v(0, 34.3) * mm, "end": v(0, -17.34) * mm, "construction": true});
            skLineSegment(sketch, "E99.0", {"start": v(35.65, 34.3) * mm, "end": v(35.65, -32.34) * mm});
            skLineSegment(sketch, "E100.MirrorCS", {"start": v(-20.71, -17) * mm, "end": v(79.12, -17) * mm});
            skLineSegment(sketch, "E101.MirrorCS", {"start": v(35, -32.81) * mm, "end": v(58.66, -15.7) * mm});
            skSolve(sketch);
        }
        {
            var Q0;
            {var subQ0=sQuery(id+"F25.wireOp",EDGE,"E97.0");var subQ1=sQuery(id+"F25.wireOp",EDGE,"E95");var subQ2=makeQuery(id+"F25.imprint","INTERSECT",VERTEX,{"derivedFrom":[subQ1,subQ0]});Q0=makeQuery(id+"F25.imprint","IMPRINT",FACE,{"disambiguationData":[TD([[makeQuery(id+"F25.imprint","IMPRINT",EDGE,{"disambiguationData":[TD([[subQ2,1.0]])],"derivedFrom":subQ1}),-1.0]])]});}
            var Q1;
            {var subQ0=sQuery(id+"F25.wireOp",EDGE,"E101.MirrorCS");var subQ1=sQuery(id+"F25.wireOp",EDGE,"E99.0");var subQ2=makeQuery(id+"F25.imprint","INTERSECT",VERTEX,{"derivedFrom":[subQ1,subQ0]});Q1=makeQuery(id+"F25.imprint","IMPRINT",FACE,{"disambiguationData":[TD([[makeQuery(id+"F25.imprint","IMPRINT",EDGE,{"disambiguationData":[TD([[subQ2,1.0]])],"derivedFrom":subQ1}),1.0]])]});}
            extrude(context, id + "F26", {"entities" : qUnion([Q0, Q1]), "operationType" : NewBodyOperationType.ADD, "endBound" : BoundingType.SYMMETRIC, "depth" : 4 * mm, "offsetDistance" : 25 * mm, "hasDraft" : true, "draftAngle" : 3 * degree});
        }
        {
            var Q0;
            Q0=qCreatedBy(makeId("Top.planeOp"),FACE);
            var sketch = newSketch(context, id + "F27", { "sketchPlane" : qUnion([Q0])});
            skLineSegment(sketch, "E102", {"start": v(0, 57.71) * mm, "end": v(0, -55.3) * mm, "construction": true});
            skLineSegment(sketch, "E103", {"start": v(-19.95, 0) * mm, "end": v(80.75, 0) * mm, "construction": true});
            skLineSegment(sketch, "E104", {"start": v(18, 30.89) * mm, "end": v(57, 17) * mm});
            skArc(sketch, "E105.trimOffspring", {"start": v(31.45, 17) * mm, "mid": v(25.68, 24.87) * mm, "end": v(18, 30.89) * mm});
            skLineSegment(sketch, "E106.trimOffspring", {"start": v(31.45, 17) * mm, "end": v(57, 17) * mm});
            skLineSegment(sketch, "E107.MirrorCS", {"start": v(18, -30.89) * mm, "end": v(57, -17) * mm});
            skArc(sketch, "E108.MirrorCS", {"start": v(31.45, -17) * mm, "mid": v(25.68, -24.87) * mm, "end": v(18, -30.89) * mm});
            skLineSegment(sketch, "E109.MirrorCS", {"start": v(31.45, -17) * mm, "end": v(57, -17) * mm});
            skSolve(sketch);
        }
        {
            var Q0;
            Q0=makeQuery(id+"F27.imprint","IMPRINT",FACE,{"disambiguationData":[TD([[makeQuery(id+"F27.imprint","IMPRINT",EDGE,{"derivedFrom":sQuery(id+"F27.wireOp",EDGE,"E104")}),-1.0]])]});
            var Q1;
            Q1=makeQuery(id+"F27.imprint","IMPRINT",FACE,{"disambiguationData":[TD([[makeQuery(id+"F27.imprint","IMPRINT",EDGE,{"derivedFrom":sQuery(id+"F27.wireOp",EDGE,"E107.MirrorCS")}),1.0]])]});
            extrude(context, id + "F28", {"entities" : qUnion([Q0, Q1]), "operationType" : NewBodyOperationType.ADD, "endBound" : BoundingType.SYMMETRIC, "depth" : 4 * mm, "offsetDistance" : 25 * mm});
        }
        {
            var Q0;
            Q0=makeQuery(id+"F28.opExtrude","CAP_EDGE",EDGE,{"disambiguationData":[OSD([sQuery(id+"F27.wireOp",EDGE,"E107.MirrorCS")])],"isStart":false});
            var Q1;
            Q1=makeQuery(id+"F28.opExtrude","CAP_EDGE",EDGE,{"disambiguationData":[OSD([sQuery(id+"F27.wireOp",EDGE,"E107.MirrorCS")])],"isStart":true});
            var Q2;
            Q2=makeQuery(id+"F26.opExtrude","CAP_EDGE",EDGE,{"disambiguationData":[OSD([sQuery(id+"F25.wireOp",EDGE,"E95")])],"isStart":false});
            var Q3;
            Q3=makeQuery(id+"F26.opExtrude","CAP_EDGE",EDGE,{"disambiguationData":[OSD([sQuery(id+"F25.wireOp",EDGE,"E95")])],"isStart":true});
            var Q4;
            Q4=makeQuery(id+"F28.opExtrude","CAP_EDGE",EDGE,{"disambiguationData":[OSD([sQuery(id+"F27.wireOp",EDGE,"E104")])],"isStart":false});
            var Q5;
            Q5=makeQuery(id+"F28.opExtrude","CAP_EDGE",EDGE,{"disambiguationData":[OSD([sQuery(id+"F27.wireOp",EDGE,"E104")])],"isStart":true});
            var Q6;
            Q6=makeQuery(id+"F26.opExtrude","CAP_EDGE",EDGE,{"disambiguationData":[OSD([sQuery(id+"F25.wireOp",EDGE,"E101.MirrorCS")])],"isStart":true});
            var Q7;
            Q7=makeQuery(id+"F26.opExtrude","CAP_EDGE",EDGE,{"disambiguationData":[OSD([sQuery(id+"F25.wireOp",EDGE,"E101.MirrorCS")])],"isStart":false});
            fillet(context, id + "F29", {"entities" : qUnion([Q0, Q1, Q2, Q3, Q4, Q5, Q6, Q7]), "radius" : 1 * mm, "tangentPropagation" : true, "allowEdgeOverflow" : false});
        }
        {
            var Q0;
            Q0=makeQuery(id+"F28.boolean.opBoolean","INTERSECT",EDGE,{"derivedFrom":[makeQuery(id+"F10.boolean.opBoolean","SPLIT",FACE,{"disambiguationData":[TD([makeQuery(id+"F2.opExtrude","SWEPT_FACE",FACE,{"disambiguationData":[OSD([sQuery(id+"F1.wireOp",EDGE,"E57.trimOffspring")])]})])],"derivedFrom":makeQuery(id+"F10.opRevolve","SWEPT_FACE",FACE,{"disambiguationData":[OSD([sQuery(id+"F9.wireOp",EDGE,"E82")])]})}),makeQuery(id+"F28.opExtrude","CAP_FACE",FACE,{"disambiguationData":[OSD([sQuery(id+"F27.wireOp",EDGE,"E104"),sQuery(id+"F27.wireOp",EDGE,"E105.trimOffspring"),sQuery(id+"F27.wireOp",EDGE,"E106.trimOffspring")])],"isStart":true})]});
            var Q1;
            Q1=makeQuery(id+"F26.boolean.opBoolean","INTERSECT",EDGE,{"derivedFrom":[makeQuery(id+"F10.boolean.opBoolean","SPLIT",FACE,{"disambiguationData":[TD([makeQuery(id+"F2.opExtrude","SWEPT_FACE",FACE,{"disambiguationData":[OSD([sQuery(id+"F1.wireOp",EDGE,"E57.trimOffspring")])]})])],"derivedFrom":makeQuery(id+"F10.opRevolve","SWEPT_FACE",FACE,{"disambiguationData":[OSD([sQuery(id+"F9.wireOp",EDGE,"E82")])]})}),makeQuery(id+"F26.opExtrude","CAP_FACE",FACE,{"disambiguationData":[OSD([sQuery(id+"F25.wireOp",EDGE,"E95"),sQuery(id+"F25.wireOp",EDGE,"E97.0"),sQuery(id+"F25.wireOp",EDGE,"E99.0")])],"isStart":true})]});
            var Q2;
            Q2=makeQuery(id+"F26.boolean.opBoolean","INTERSECT",EDGE,{"derivedFrom":[makeQuery(id+"F10.boolean.opBoolean","SPLIT",FACE,{"disambiguationData":[TD([makeQuery(id+"F2.opExtrude","SWEPT_FACE",FACE,{"disambiguationData":[OSD([sQuery(id+"F1.wireOp",EDGE,"E57.trimOffspring")])]})])],"derivedFrom":makeQuery(id+"F10.opRevolve","SWEPT_FACE",FACE,{"disambiguationData":[OSD([sQuery(id+"F9.wireOp",EDGE,"E82")])]})}),makeQuery(id+"F26.opExtrude","CAP_FACE",FACE,{"disambiguationData":[OSD([sQuery(id+"F25.wireOp",EDGE,"E95"),sQuery(id+"F25.wireOp",EDGE,"E97.0"),sQuery(id+"F25.wireOp",EDGE,"E99.0")])],"isStart":false})]});
            var Q3;
            Q3=makeQuery(id+"F28.boolean.opBoolean","INTERSECT",EDGE,{"derivedFrom":[makeQuery(id+"F10.boolean.opBoolean","SPLIT",FACE,{"disambiguationData":[TD([makeQuery(id+"F2.opExtrude","SWEPT_FACE",FACE,{"disambiguationData":[OSD([sQuery(id+"F1.wireOp",EDGE,"E57.trimOffspring")])]})])],"derivedFrom":makeQuery(id+"F10.opRevolve","SWEPT_FACE",FACE,{"disambiguationData":[OSD([sQuery(id+"F9.wireOp",EDGE,"E82")])]})}),makeQuery(id+"F28.opExtrude","CAP_FACE",FACE,{"disambiguationData":[OSD([sQuery(id+"F27.wireOp",EDGE,"E107.MirrorCS"),sQuery(id+"F27.wireOp",EDGE,"E108.MirrorCS"),sQuery(id+"F27.wireOp",EDGE,"E109.MirrorCS")])],"isStart":false})]});
            var Q4;
            Q4=makeQuery(id+"F26.boolean.opBoolean","INTERSECT",EDGE,{"derivedFrom":[makeQuery(id+"F10.boolean.opBoolean","SPLIT",FACE,{"disambiguationData":[TD([makeQuery(id+"F2.opExtrude","SWEPT_FACE",FACE,{"disambiguationData":[OSD([sQuery(id+"F1.wireOp",EDGE,"E57.trimOffspring")])]})])],"derivedFrom":makeQuery(id+"F10.opRevolve","SWEPT_FACE",FACE,{"disambiguationData":[OSD([sQuery(id+"F9.wireOp",EDGE,"E82")])]})}),makeQuery(id+"F26.opExtrude","CAP_FACE",FACE,{"disambiguationData":[OSD([sQuery(id+"F25.wireOp",EDGE,"E99.0"),sQuery(id+"F25.wireOp",EDGE,"E100.MirrorCS"),sQuery(id+"F25.wireOp",EDGE,"E101.MirrorCS")])],"isStart":false})]});
            var Q5;
            Q5=makeQuery(id+"F26.boolean.opBoolean","INTERSECT",EDGE,{"derivedFrom":[makeQuery(id+"F10.boolean.opBoolean","SPLIT",FACE,{"disambiguationData":[TD([makeQuery(id+"F2.opExtrude","SWEPT_FACE",FACE,{"disambiguationData":[OSD([sQuery(id+"F1.wireOp",EDGE,"E57.trimOffspring")])]})])],"derivedFrom":makeQuery(id+"F10.opRevolve","SWEPT_FACE",FACE,{"disambiguationData":[OSD([sQuery(id+"F9.wireOp",EDGE,"E82")])]})}),makeQuery(id+"F26.opExtrude","CAP_FACE",FACE,{"disambiguationData":[OSD([sQuery(id+"F25.wireOp",EDGE,"E99.0"),sQuery(id+"F25.wireOp",EDGE,"E100.MirrorCS"),sQuery(id+"F25.wireOp",EDGE,"E101.MirrorCS")])],"isStart":true})]});
            fillet(context, id + "F30", {"entities" : qUnion([Q0, Q1, Q2, Q3, Q4, Q5]), "radius" : 2 * mm, "tangentPropagation" : true, "allowEdgeOverflow" : false});
        }
    });
